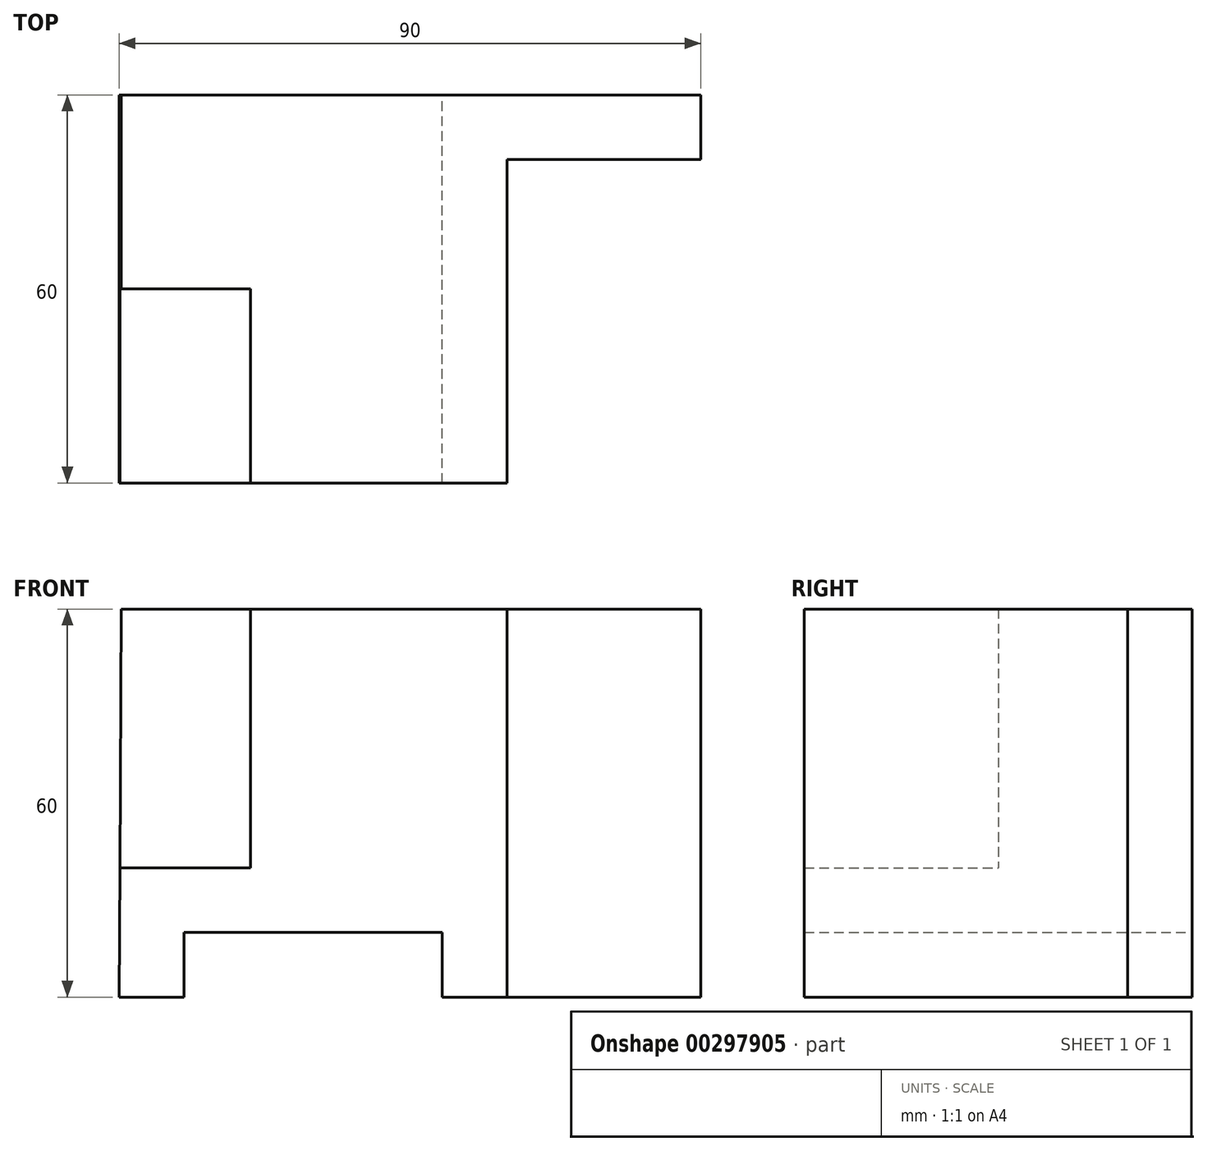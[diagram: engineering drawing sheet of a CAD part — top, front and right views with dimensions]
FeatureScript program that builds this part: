
annotation { "Feature Type Name" : "Feature", "Feature Type Description" : "" }
export const myFeature = defineFeature(function(context is Context, id is Id, definition is map)
    precondition{}
    {
        {
            var Q0;
            Q0=qCreatedBy(makeId("Front.planeOp"),FACE);
            var sketch = newSketch(context, id + "F0", { "sketchPlane" : qUnion([Q0])});
            skLineSegment(sketch, "E0", {"start": v(72.81, 29.7) * mm, "end": v(72.81, -30.3) * mm});
            skLineSegment(sketch, "E1", {"start": v(72.81, 29.7) * mm, "end": v(42.81, 29.7) * mm});
            skLineSegment(sketch, "E2", {"start": v(42.81, 29.7) * mm, "end": v(42.81, -30.3) * mm});
            skLineSegment(sketch, "E3", {"start": v(42.81, -30.3) * mm, "end": v(72.81, -30.3) * mm});
            skLineSegment(sketch, "E4", {"start": v(42.81, -30.3) * mm, "end": v(32.81, -30.3) * mm});
            skLineSegment(sketch, "E5", {"start": v(32.81, -30.3) * mm, "end": v(32.81, -20.3) * mm});
            skLineSegment(sketch, "E6", {"start": v(32.81, -20.3) * mm, "end": v(-7.19, -20.3) * mm});
            skLineSegment(sketch, "E7", {"start": v(-7.19, -20.3) * mm, "end": v(-7.19, -30.3) * mm});
            skLineSegment(sketch, "E8", {"start": v(-7.19, -30.3) * mm, "end": v(-17.19, -30.3) * mm});
            skLineSegment(sketch, "E9", {"start": v(42.81, 29.7) * mm, "end": v(3.14, 29.7) * mm});
            skLineSegment(sketch, "E10", {"start": v(3.14, 29.7) * mm, "end": v(-16.86, 29.7) * mm});
            skLineSegment(sketch, "E11", {"start": v(-16.86, 29.7) * mm, "end": v(-17.19, -30.3) * mm});
            skLineSegment(sketch, "E12", {"start": v(-17.08, -10.3) * mm, "end": v(3.14, -10.3) * mm});
            skLineSegment(sketch, "E13", {"start": v(3.14, 29.7) * mm, "end": v(3.14, -10.3) * mm});
            skSolve(sketch);
        }
        {
            var Q0;
            Q0=makeQuery(id+"F0.imprint","IMPRINT",FACE,{"disambiguationData":[TD([[makeQuery(id+"F0.imprint","IMPRINT",EDGE,{"derivedFrom":sQuery(id+"F0.wireOp",EDGE,"E2")}),-1.0]])]});
            extrude(context, id + "F1", {"entities" : qUnion([Q0]), "depth" : 60 * mm});
        }
        {
            var Q0;
            {var subQ0=sQuery(id+"F0.wireOp",EDGE,"E10");Q0=makeQuery(id+"F0.imprint","IMPRINT",FACE,{"disambiguationData":[TD([[makeQuery(id+"F0.imprint","IMPRINT",EDGE,{"derivedFrom":subQ0}),1.0]])]});}
            extrude(context, id + "F2", {"entities" : qUnion([Q0]), "operationType" : NewBodyOperationType.ADD, "depth" : 30 * mm});
        }
        {
            var Q0;
            Q0=makeQuery(id+"F0.imprint","IMPRINT",FACE,{"disambiguationData":[TD([[makeQuery(id+"F0.imprint","IMPRINT",EDGE,{"derivedFrom":sQuery(id+"F0.wireOp",EDGE,"E0")}),-1.0]])]});
            extrude(context, id + "F3", {"entities" : qUnion([Q0]), "operationType" : NewBodyOperationType.ADD, "depth" : 10 * mm});
        }
    });
